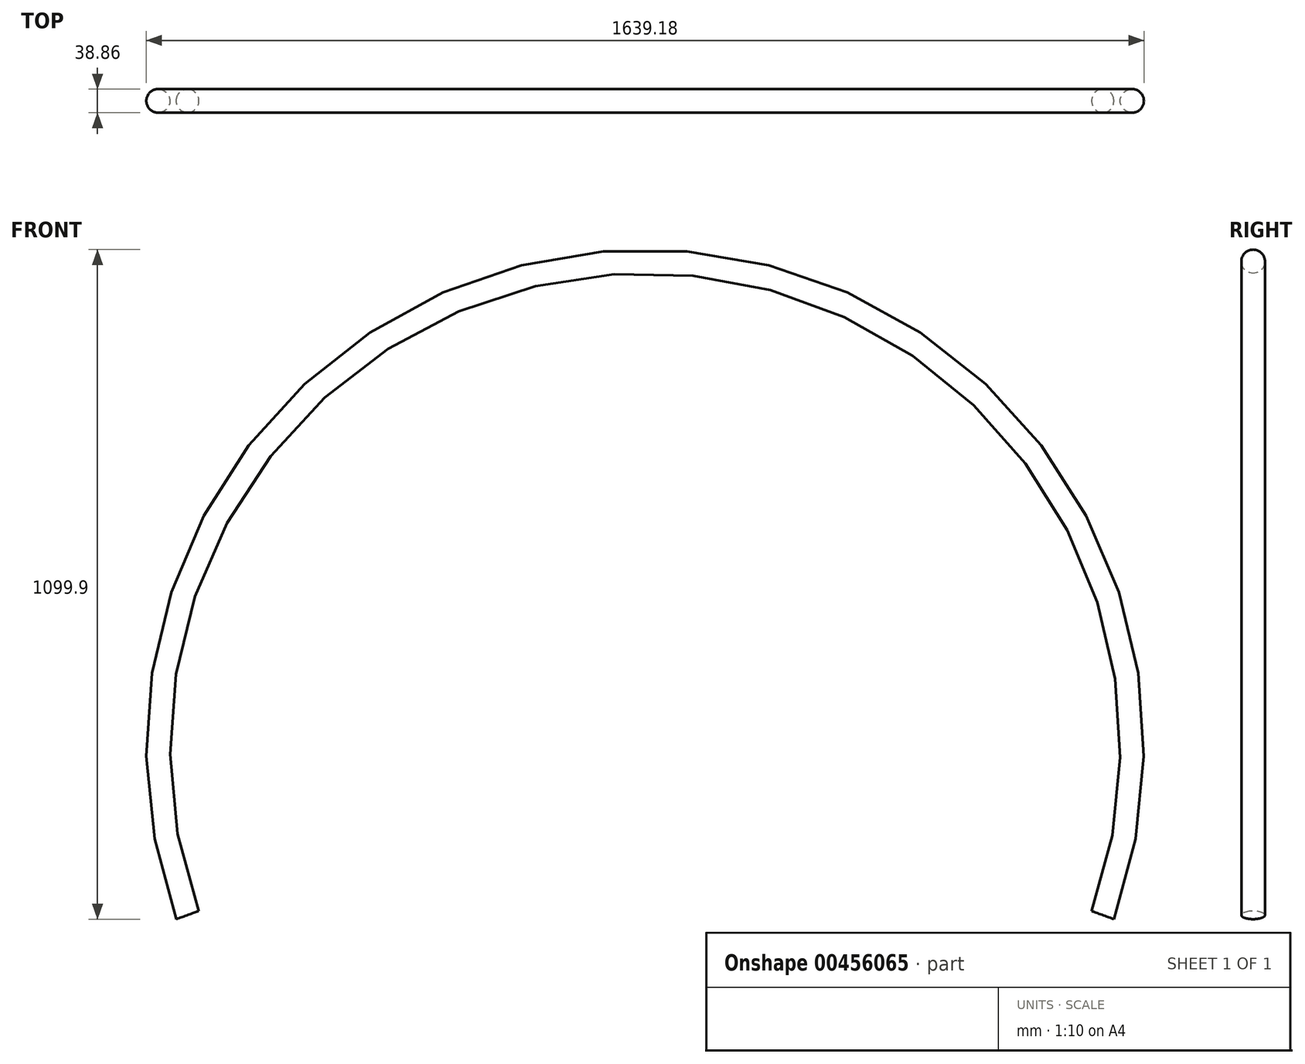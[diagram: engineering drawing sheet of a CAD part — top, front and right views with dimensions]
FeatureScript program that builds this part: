
annotation { "Feature Type Name" : "Feature", "Feature Type Description" : "" }
export const myFeature = defineFeature(function(context is Context, id is Id, definition is map)
    precondition{}
    {
        {
            var Q0;
            Q0=qCreatedBy(makeId("Top.planeOp"),FACE);
            var sketch = newSketch(context, id + "F0", { "sketchPlane" : qUnion([Q0])});
            skLineSegment(sketch, "E0", {"start": v(0, 0) * mm, "end": v(800.15, 0) * mm});
            skCircle(sketch, "E1", {"center": v(800.15, 0) * mm, "radius": 19.43 * mm});
            skLineSegment(sketch, "E2", {"start": v(0, 18.17) * mm, "end": v(0, -26.19) * mm});
            skSolve(sketch);
        }
        {
            var Q0;
            Q0=makeQuery(id+"F0.imprint","IMPRINT",FACE,{"disambiguationData":[TD([[makeQuery(id+"F0.imprint","IMPRINT",EDGE,{"derivedFrom":sQuery(id+"F0.wireOp",EDGE,"E1")}),1.0]])]});
            var Q1;
            Q1=sQuery(id+"F0.wireOp",EDGE,"E2");
            revolve(context, id + "F1", {"entities" : qUnion([Q0]), "axis" : qUnion([Q1]), "revolveType" : RevolveType.TWO_DIRECTIONS, "oppositeDirection" : true, "angle" : 20 * degree, "angleBack" : 160 * degree});
        }
    });
